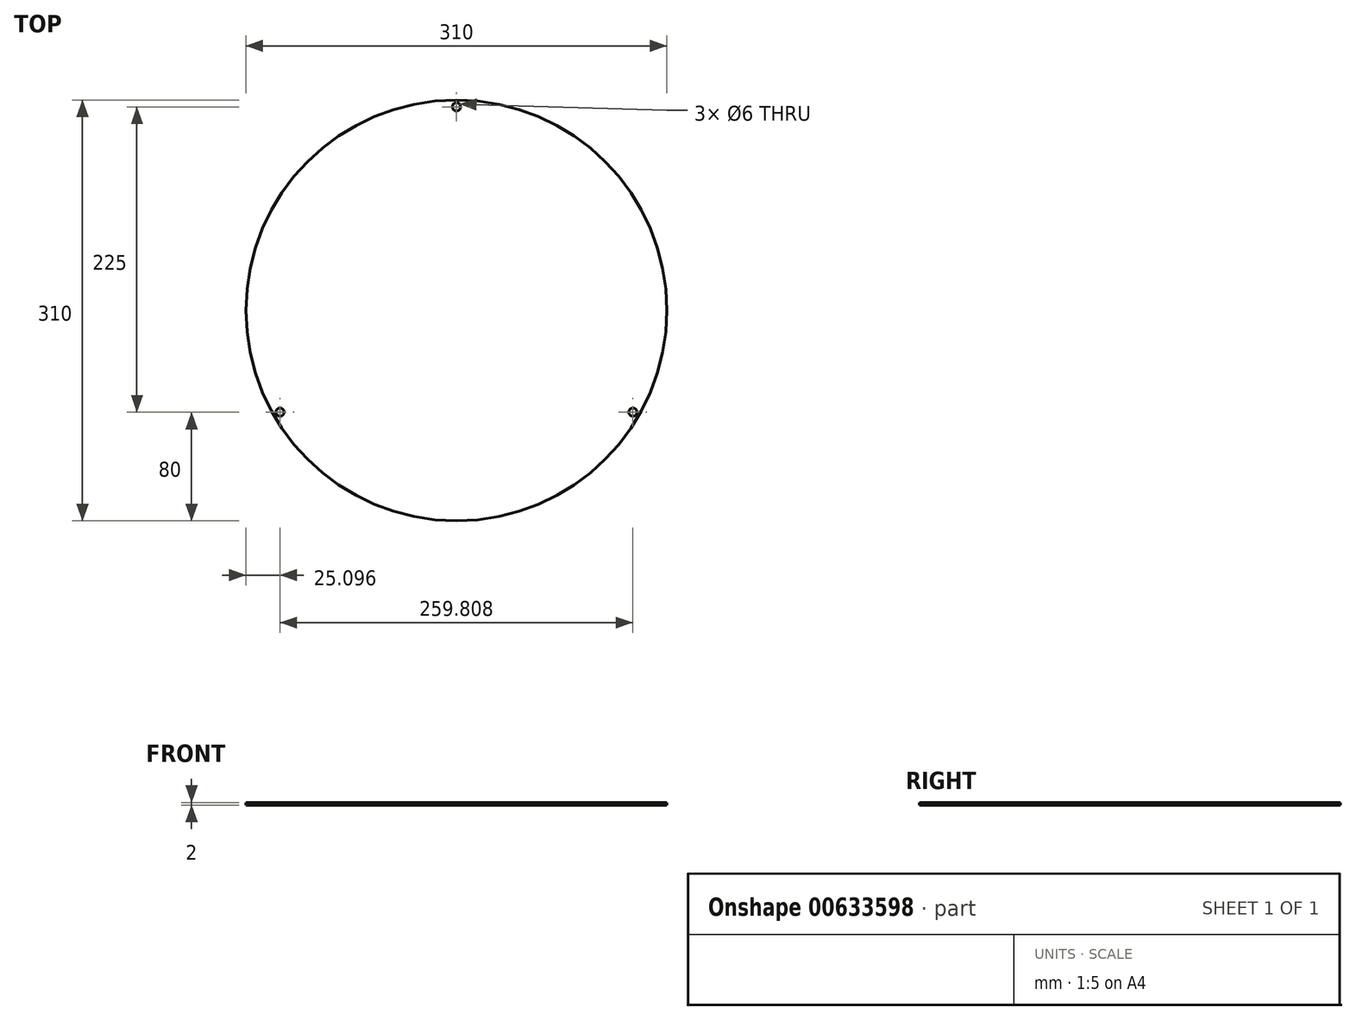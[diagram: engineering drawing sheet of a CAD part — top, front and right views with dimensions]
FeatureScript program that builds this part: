
annotation { "Feature Type Name" : "Feature", "Feature Type Description" : "" }
export const myFeature = defineFeature(function(context is Context, id is Id, definition is map)
    precondition{}
    {
        {
            var Q0;
            Q0=qCreatedBy(makeId("Top.planeOp"),FACE);
            var sketch = newSketch(context, id + "F0", { "sketchPlane" : qUnion([Q0])});
            skCircle(sketch, "E0", {"center": v(0, 0) * mm, "radius": 155 * mm});
            skCircle(sketch, "E1", {"center": v(0, 0) * mm, "radius": 150 * mm, "construction": true});
            skCircle(sketch, "E2", {"center": v(0, 150) * mm, "radius": 3 * mm});
            skCircle(sketch, "E3.1.0", {"center": v(-129.9, -75) * mm, "radius": 3 * mm});
            skCircle(sketch, "E3.2.0", {"center": v(129.9, -75) * mm, "radius": 3 * mm});
            skSolve(sketch);
        }
        {
            var Q0;
            Q0=qSketchRegion(id+"F0",true);
            extrude(context, id + "F1", {"entities" : qUnion([Q0]), "depth" : 2 * mm, "offsetDistance" : 25 * mm});
        }
    });
